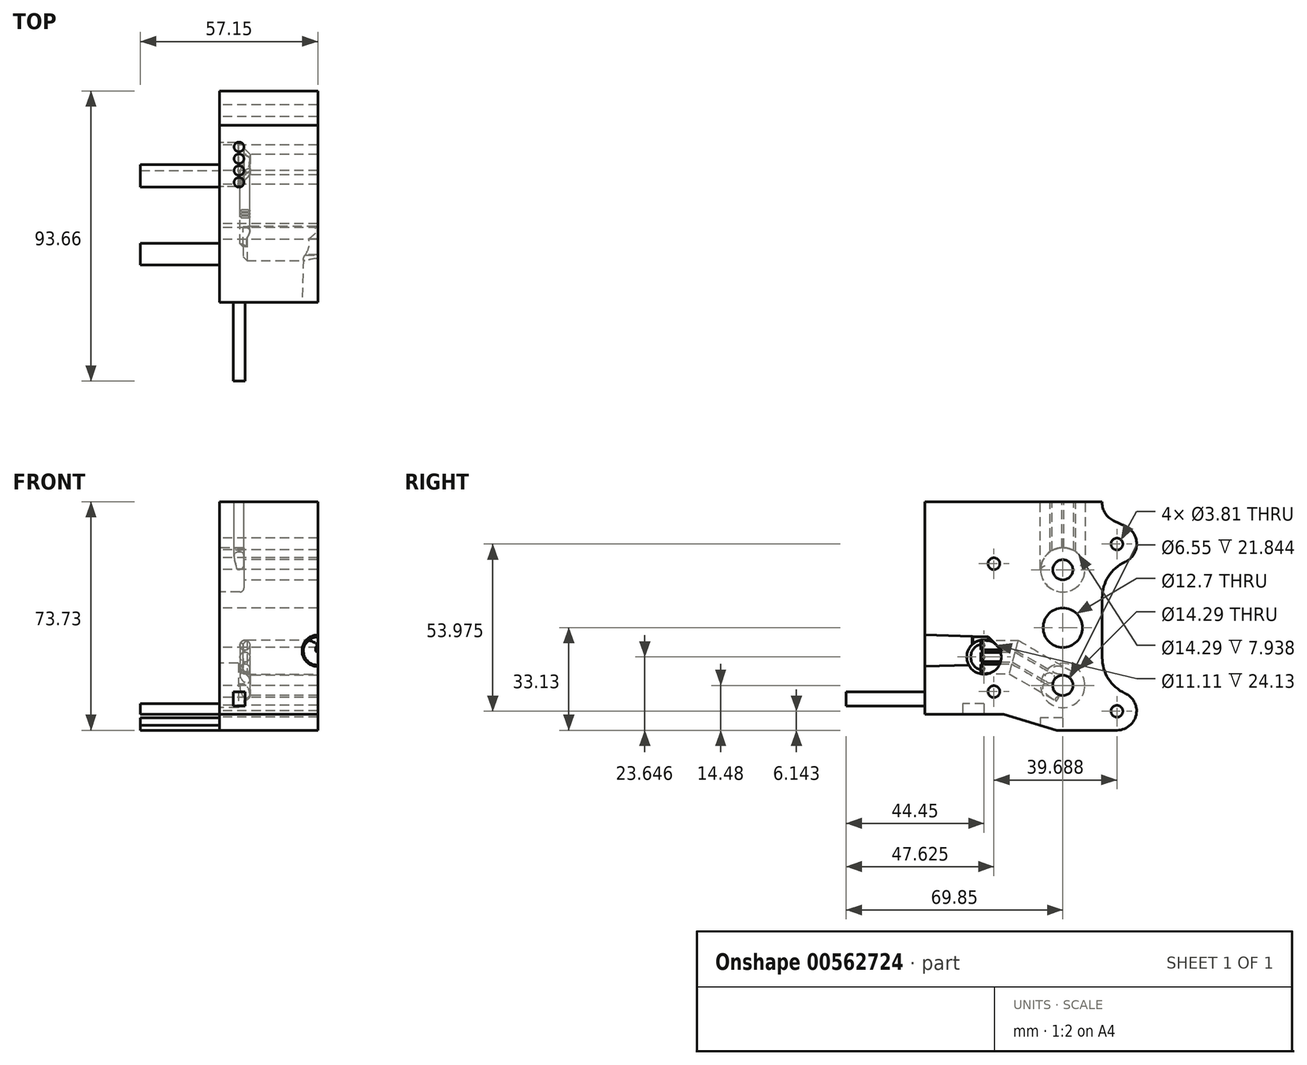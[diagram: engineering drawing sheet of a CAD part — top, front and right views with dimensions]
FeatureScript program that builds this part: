
annotation { "Feature Type Name" : "Feature", "Feature Type Description" : "" }
export const myFeature = defineFeature(function(context is Context, id is Id, definition is map)
    precondition{}
    {
        {
            var Q0;
            Q0=qCreatedBy(makeId("Front.planeOp"),FACE);
            var sketch = newSketch(context, id + "F0", { "sketchPlane" : qUnion([Q0])});
            skLineSegment(sketch, "E0.bottom", {"start": v(-31.75, 40.6) * mm, "end": v(31.75, 40.6) * mm});
            skLineSegment(sketch, "E0.top", {"start": v(-31.75, -35.6) * mm, "end": v(31.75, -35.6) * mm});
            skLineSegment(sketch, "E0.left", {"start": v(-31.75, 40.6) * mm, "end": v(-31.75, -35.6) * mm});
            skLineSegment(sketch, "E0.right", {"start": v(31.75, 40.6) * mm, "end": v(31.75, -35.6) * mm});
            skSolve(sketch);
        }
        {
            var Q0;
            Q0=makeQuery(id+"F0.imprint","IMPRINT",FACE,{"disambiguationData":[TD([[makeQuery(id+"F0.imprint","IMPRINT",EDGE,{"derivedFrom":sQuery(id+"F0.wireOp",EDGE,"E0.bottom")}),-1.0]])]});
            extrude(context, id + "F1", {"entities" : qUnion([Q0]), "depth" : 76.2 * mm, "offsetDistance" : 25.4 * mm});
        }
        {
            var Q0;
            Q0=makeQuery(id+"F1.opExtrude","SWEPT_FACE",FACE,{"disambiguationData":[OSD([sQuery(id+"F0.wireOp",EDGE,"E0.left")])]});
            var sketch = newSketch(context, id + "F2", { "sketchPlane" : qUnion([Q0])});
            skCircle(sketch, "E1", {"center": v(31.75, 0) * mm, "radius": 6.35 * mm});
            skCircle(sketch, "E2", {"center": v(31.75, 18.66) * mm, "radius": 7.14 * mm});
            skCircle(sketch, "E3", {"center": v(31.75, -18.65) * mm, "radius": 7.14 * mm});
            skCircle(sketch, "E4", {"center": v(14.29, 26.99) * mm, "radius": 1.9 * mm});
            skCircle(sketch, "E5", {"center": v(14.29, -26.99) * mm, "radius": 1.9 * mm});
            skCircle(sketch, "E6", {"center": v(53.98, -20.64) * mm, "radius": 1.9 * mm});
            skCircle(sketch, "E7", {"center": v(53.97, 20.64) * mm, "radius": 1.9 * mm});
            skCircle(sketch, "E8", {"center": v(31.75, 18.66) * mm, "radius": 3.25 * mm});
            skCircle(sketch, "E9", {"center": v(31.75, -18.65) * mm, "radius": 3.28 * mm});
            skLineSegment(sketch, "E10.bottom", {"start": v(31.75, -29.15) * mm, "end": v(39.04, -29.15) * mm});
            skLineSegment(sketch, "E10.top", {"start": v(31.75, -33.13) * mm, "end": v(39.04, -33.13) * mm});
            skLineSegment(sketch, "E10.left", {"start": v(31.75, -29.15) * mm, "end": v(31.75, -33.13) * mm});
            skLineSegment(sketch, "E10.right", {"start": v(39.04, -29.15) * mm, "end": v(39.04, -33.13) * mm});
            skLineSegment(sketch, "E11.bottom", {"start": v(57.15, -24.55) * mm, "end": v(64.1, -24.55) * mm});
            skLineSegment(sketch, "E11.top", {"start": v(57.15, -30.95) * mm, "end": v(64.1, -30.95) * mm});
            skLineSegment(sketch, "E11.left", {"start": v(57.15, -24.55) * mm, "end": v(57.15, -30.95) * mm});
            skLineSegment(sketch, "E11.right", {"start": v(64.1, -24.55) * mm, "end": v(64.1, -30.95) * mm});
            skCircle(sketch, "E12", {"center": v(31.75, -18.65) * mm, "radius": 5.56 * mm});
            skLineSegment(sketch, "E13", {"start": v(25.4, -35.6) * mm, "end": v(50.8, -27.98) * mm});
            skLineSegment(sketch, "E14", {"start": v(50.8, -27.98) * mm, "end": v(76.2, -27.98) * mm});
            skSolve(sketch);
        }
        {
            var Q0;
            Q0=makeQuery(id+"F2.imprint","IMPRINT",FACE,{"disambiguationData":[TD([[makeQuery(id+"F2.imprint","IMPRINT",EDGE,{"derivedFrom":sQuery(id+"F2.wireOp",EDGE,"E8")}),1.0]])]});
            var Q1;
            Q1=makeQuery(id+"F2.imprint","IMPRINT",FACE,{"disambiguationData":[TD([[makeQuery(id+"F2.imprint","IMPRINT",EDGE,{"derivedFrom":sQuery(id+"F2.wireOp",EDGE,"E4")}),1.0]])]});
            var Q2;
            Q2=makeQuery(id+"F2.imprint","IMPRINT",FACE,{"disambiguationData":[TD([[makeQuery(id+"F2.imprint","IMPRINT",EDGE,{"derivedFrom":sQuery(id+"F2.wireOp",EDGE,"E5")}),1.0]])]});
            var Q3;
            Q3=makeQuery(id+"F2.imprint","IMPRINT",FACE,{"disambiguationData":[TD([[makeQuery(id+"F2.imprint","IMPRINT",EDGE,{"derivedFrom":sQuery(id+"F2.wireOp",EDGE,"E9")}),1.0]])]});
            var Q4;
            Q4=makeQuery(id+"F2.imprint","IMPRINT",FACE,{"disambiguationData":[TD([[makeQuery(id+"F2.imprint","IMPRINT",EDGE,{"derivedFrom":sQuery(id+"F2.wireOp",EDGE,"E6")}),1.0]])]});
            var Q5;
            Q5=makeQuery(id+"F2.imprint","IMPRINT",FACE,{"disambiguationData":[TD([[makeQuery(id+"F2.imprint","IMPRINT",EDGE,{"derivedFrom":sQuery(id+"F2.wireOp",EDGE,"E7")}),1.0]])]});
            var Q6;
            Q6=makeQuery(id+"F2.imprint","IMPRINT",FACE,{"disambiguationData":[TD([[makeQuery(id+"F2.imprint","IMPRINT",EDGE,{"derivedFrom":sQuery(id+"F2.wireOp",EDGE,"E1")}),1.0]])]});
            extrude(context, id + "F3", {"entities" : qUnion([Q0, Q1, Q2, Q3, Q4, Q5, Q6]), "operationType" : NewBodyOperationType.REMOVE, "endBound" : BoundingType.THROUGH_ALL, "oppositeDirection" : true, "depth" : 25.4 * mm, "offsetDistance" : 25.4 * mm});
        }
        {
            var Q0;
            Q0=makeQuery(id+"F2.imprint","IMPRINT",FACE,{"disambiguationData":[TD([[makeQuery(id+"F2.imprint","IMPRINT",EDGE,{"derivedFrom":sQuery(id+"F2.wireOp",EDGE,"E10.bottom")}),-1.0]])]});
            extrude(context, id + "F4", {"entities" : qUnion([Q0]), "depth" : 25.4 * mm, "offsetDistance" : 25.4 * mm});
        }
        {
            var Q0;
            Q0=makeQuery(id+"F2.imprint","IMPRINT",FACE,{"disambiguationData":[TD([[makeQuery(id+"F2.imprint","IMPRINT",EDGE,{"derivedFrom":sQuery(id+"F2.wireOp",EDGE,"E11.bottom")}),-1.0]])]});
            extrude(context, id + "F5", {"entities" : qUnion([Q0]), "depth" : 25.4 * mm, "offsetDistance" : 25.4 * mm});
        }
        {
            var Q0;
            Q0=makeQuery(id+"F1.opExtrude","CAP_FACE",FACE,{"disambiguationData":[OSD([sQuery(id+"F0.wireOp",EDGE,"E0.bottom"),sQuery(id+"F0.wireOp",EDGE,"E0.top"),sQuery(id+"F0.wireOp",EDGE,"E0.left"),sQuery(id+"F0.wireOp",EDGE,"E0.right")])],"isStart":false});
            var sketch = newSketch(context, id + "F6", { "sketchPlane" : qUnion([Q0])});
            skLineSegment(sketch, "E15.bottom", {"start": v(-27.25, -20.74) * mm, "end": v(-23.5, -20.74) * mm});
            skLineSegment(sketch, "E15.top", {"start": v(-27.25, -25.26) * mm, "end": v(-23.5, -25.26) * mm});
            skLineSegment(sketch, "E15.left", {"start": v(-27.25, -20.74) * mm, "end": v(-27.25, -25.26) * mm});
            skLineSegment(sketch, "E15.right", {"start": v(-23.5, -20.74) * mm, "end": v(-23.5, -25.26) * mm});
            skSolve(sketch);
        }
        {
            var Q0;
            Q0=makeQuery(id+"F6.imprint","IMPRINT",FACE,{"disambiguationData":[TD([[makeQuery(id+"F6.imprint","IMPRINT",EDGE,{"derivedFrom":sQuery(id+"F6.wireOp",EDGE,"E15.bottom")}),-1.0]])]});
            extrude(context, id + "F7", {"entities" : qUnion([Q0]), "depth" : 25.4 * mm, "offsetDistance" : 25.4 * mm});
        }
        {
            var Q0;
            Q0=makeQuery(id+"F4.opExtrude","SWEPT_FACE",FACE,{"disambiguationData":[OSD([sQuery(id+"F2.wireOp",EDGE,"E10.left")])]});
            var sketch = newSketch(context, id + "F8", { "sketchPlane" : qUnion([Q0])});
            skLineSegment(sketch, "E16", {"start": v(31.75, -18.65) * mm, "end": v(23.5, -18.65) * mm});
            skSolve(sketch);
        }
        {
            var Q0;
            Q0=makeQuery(id+"F7.opExtrude","SWEPT_FACE",FACE,{"disambiguationData":[OSD([sQuery(id+"F6.wireOp",EDGE,"E15.right")])]});
            var sketch = newSketch(context, id + "F9", { "sketchPlane" : qUnion([Q0])});
            skLineSegment(sketch, "E17", {"start": v(-31.75, -18.65) * mm, "end": v(-47.62, -9.48) * mm});
            skLineSegment(sketch, "E18", {"start": v(-47.62, -9.48) * mm, "end": v(-57.15, -9.48) * mm});
            skLineSegment(sketch, "E19", {"start": v(-29.92, -15.3) * mm, "end": v(-46.6, -5.67) * mm});
            skLineSegment(sketch, "E20", {"start": v(-33.04, -22.3) * mm, "end": v(-48.65, -13.3) * mm});
            skLineSegment(sketch, "E21", {"start": v(-46.6, -5.67) * mm, "end": v(-57.15, -5.67) * mm});
            skLineSegment(sketch, "E22", {"start": v(-48.65, -13.3) * mm, "end": v(-57.15, -13.3) * mm});
            skSolve(sketch);
        }
        {
            var Q0;
            Q0=makeQuery(id+"F5.opExtrude","SWEPT_FACE",FACE,{"disambiguationData":[OSD([sQuery(id+"F2.wireOp",EDGE,"E11.left")])]});
            var sketch = newSketch(context, id + "F10", { "sketchPlane" : qUnion([Q0])});
            skLineSegment(sketch, "E23", {"start": v(23.5, -9.48) * mm, "end": v(0, -9.48) * mm});
            skCircle(sketch, "E24", {"center": v(23.5, -9.48) * mm, "radius": 1.59 * mm});
            skCircle(sketch, "E25", {"center": v(23.5, -5.67) * mm, "radius": 1.59 * mm});
            skCircle(sketch, "E26", {"center": v(23.5, -13.3) * mm, "radius": 1.59 * mm});
            skSolve(sketch);
        }
        {
            var Q0;
            Q0=makeQuery(id+"F2.imprint","IMPRINT",FACE,{"disambiguationData":[TD([[makeQuery(id+"F2.imprint","IMPRINT",EDGE,{"derivedFrom":sQuery(id+"F2.wireOp",EDGE,"E3")}),1.0]])]});
            var Q1;
            Q1=makeQuery(id+"F2.imprint","IMPRINT",FACE,{"disambiguationData":[TD([[makeQuery(id+"F2.imprint","IMPRINT",EDGE,{"derivedFrom":sQuery(id+"F2.wireOp",EDGE,"E9")}),-1.0]])]});
            var Q2;
            Q2=sQuery(id+"F9.wireOp",VERTEX,"E17.start");
            extrude(context, id + "F11", {"entities" : qUnion([Q0, Q1]), "operationType" : NewBodyOperationType.REMOVE, "oppositeDirection" : true, "depth" : 9.9 * mm, "endBoundEntityVertex" : qUnion([Q2]), "offsetDistance" : 25.4 * mm});
        }
        {
            var Q0;
            Q0=makeQuery(id+"F11.boolean.opBoolean","COPY",EDGE,{"derivedFrom":makeQuery(id+"F11.opExtrude","CAP_EDGE",EDGE,{"disambiguationData":[OSD([sQuery(id+"F2.wireOp",EDGE,"E3")])],"isStart":false})});
            chamfer(context, id + "F12", {"entities" : qUnion([Q0]), "width" : 3.8 * mm, "tangentPropagation" : true});
        }
        {
            var Q0;
            {var subQ0=sQuery(id+"F2.wireOp",EDGE,"E10.right");var subQ1=sQuery(id+"F2.wireOp",EDGE,"E10.top");var subQ2=makeQuery(id+"F2.imprint","INTERSECT",VERTEX,{"derivedFrom":[subQ1,subQ0]});Q0=makeQuery(id+"F2.imprint","IMPRINT",FACE,{"disambiguationData":[TD([[makeQuery(id+"F2.imprint","IMPRINT",EDGE,{"disambiguationData":[TD([[subQ2,1.0]])],"derivedFrom":subQ1}),1.0]])]});}
            var Q1;
            {var subQ11=sQuery(id+"F2.wireOp",EDGE,"E11.top");Q1=makeQuery(id+"F2.imprint","IMPRINT",FACE,{"disambiguationData":[TD([[makeQuery(id+"F2.imprint","IMPRINT",EDGE,{"derivedFrom":subQ11}),-1.0]])]});}
            var Q2;
            {var subQ0=sQuery(id+"F2.wireOp",EDGE,"E11.top");Q2=makeQuery(id+"F2.imprint","IMPRINT",FACE,{"disambiguationData":[TD([[makeQuery(id+"F2.imprint","IMPRINT",EDGE,{"derivedFrom":subQ0}),1.0]])]});}
            extrude(context, id + "F13", {"entities" : qUnion([Q0, Q1, Q2]), "operationType" : NewBodyOperationType.REMOVE, "endBound" : BoundingType.THROUGH_ALL, "oppositeDirection" : true, "depth" : 25.4 * mm, "offsetDistance" : 25.4 * mm});
        }
        {
            var Q0;
            Q0=makeQuery(id+"F1.opExtrude","CAP_FACE",FACE,{"disambiguationData":[OSD([sQuery(id+"F0.wireOp",EDGE,"E0.bottom"),sQuery(id+"F0.wireOp",EDGE,"E0.top"),sQuery(id+"F0.wireOp",EDGE,"E0.left"),sQuery(id+"F0.wireOp",EDGE,"E0.right")])],"isStart":false});
            var sketch = newSketch(context, id + "F14", { "sketchPlane" : qUnion([Q0])});
            skCircle(sketch, "E27", {"center": v(0, -7.45) * mm, "radius": 4.45 * mm});
            skCircle(sketch, "E28", {"center": v(0, 9.57) * mm, "radius": 3.81 * mm});
            skSolve(sketch);
        }
        {
            var Q0;
            Q0=makeQuery(id+"F14.imprint","IMPRINT",FACE,{"disambiguationData":[TD([[makeQuery(id+"F14.imprint","IMPRINT",EDGE,{"derivedFrom":sQuery(id+"F14.wireOp",EDGE,"E27")}),1.0]])]});
            extrude(context, id + "F15", {"entities" : qUnion([Q0]), "operationType" : NewBodyOperationType.REMOVE, "oppositeDirection" : true, "depth" : 24.76 * mm, "offsetDistance" : 25.4 * mm});
        }
        {
            var Q0;
            Q0=qCreatedBy(makeId("Right.planeOp"),FACE);
            var sketch = newSketch(context, id + "F16", { "sketchPlane" : qUnion([Q0])});
            skLineSegment(sketch, "E29", {"start": v(-76.17, -12.53) * mm, "end": v(-60.94, -12.06) * mm});
            skLineSegment(sketch, "E30", {"start": v(-60.94, -12.06) * mm, "end": v(-60.15, -11.26) * mm});
            skLineSegment(sketch, "E31", {"start": v(-76.2, -11.26) * mm, "end": v(-60.15, -11.26) * mm});
            skLineSegment(sketch, "E32", {"start": v(-76.2, -7.45) * mm, "end": v(-74.2, -7.45) * mm});
            skLineSegment(sketch, "E33", {"start": v(-76.17, -12.53) * mm, "end": v(-76.34, -12.54) * mm});
            skLineSegment(sketch, "E34", {"start": v(-76.34, -12.54) * mm, "end": v(-76.34, -11.26) * mm});
            skLineSegment(sketch, "E35", {"start": v(-76.34, -11.26) * mm, "end": v(-76.2, -11.26) * mm});
            skSolve(sketch);
        }
        {
            var Q0;
            Q0 = qSketchRegion(id + "F16", true);
            var Q1;
            Q1=sQuery(id+"F16.wireOp",EDGE,"E32");
            revolve(context, id + "F17", {"operationType" : NewBodyOperationType.REMOVE, "entities" : qUnion([Q0]), "axis" : qUnion([Q1]), "revolveType" : RevolveType.FULL, "oppositeDirection" : true});
        }
        {
            var Q0;
            Q0=makeQuery(id+"F1.opExtrude","SWEPT_FACE",FACE,{"disambiguationData":[OSD([sQuery(id+"F0.wireOp",EDGE,"E0.right")])]});
            extrude(context, id + "F18", {"entities" : qUnion([Q0]), "operationType" : NewBodyOperationType.REMOVE, "oppositeDirection" : true, "depth" : 31.75 * mm, "offsetDistance" : 25.4 * mm});
        }
        {
            var Q0;
            Q0=makeQuery(id+"F15.boolean.opBoolean","COPY",EDGE,{"derivedFrom":makeQuery(id+"F15.opExtrude","CAP_EDGE",EDGE,{"disambiguationData":[OSD([sQuery(id+"F14.wireOp",EDGE,"E27")])],"isStart":false})});
            chamfer(context, id + "F19", {"entities" : qUnion([Q0]), "width" : 4.32 * mm, "tangentPropagation" : true});
        }
        {
            var Q0;
            Q0=makeQuery(id+"F4.opExtrude","SWEPT_FACE",FACE,{"disambiguationData":[OSD([sQuery(id+"F2.wireOp",EDGE,"E10.left")])]});
            var sketch = newSketch(context, id + "F20", { "sketchPlane" : qUnion([Q0])});
            skLineSegment(sketch, "E36", {"start": v(31.75, 18.66) * mm, "end": v(25.4, 18.66) * mm});
            skLineSegment(sketch, "E37", {"start": v(25.4, 18.66) * mm, "end": v(25.4, 40.6) * mm});
            skSolve(sketch);
        }
        {
            var Q0;
            Q0=makeQuery(id+"F1.opExtrude","SWEPT_FACE",FACE,{"disambiguationData":[OSD([sQuery(id+"F0.wireOp",EDGE,"E0.bottom")])]});
            var sketch = newSketch(context, id + "F21", { "sketchPlane" : qUnion([Q0])});
            skCircle(sketch, "E38", {"center": v(-25.4, -29.84) * mm, "radius": 1.59 * mm});
            skCircle(sketch, "E39", {"center": v(-25.4, -33.65) * mm, "radius": 1.59 * mm});
            skCircle(sketch, "E40", {"center": v(-25.4, -26.04) * mm, "radius": 1.59 * mm});
            skCircle(sketch, "E41", {"center": v(-25.4, -37.46) * mm, "radius": 1.59 * mm});
            skSolve(sketch);
        }
        {
            var Q0;
            Q0=makeQuery(id+"F21.imprint","IMPRINT",FACE,{"disambiguationData":[TD([[makeQuery(id+"F21.imprint","IMPRINT",EDGE,{"derivedFrom":sQuery(id+"F21.wireOp",EDGE,"E40")}),1.0]])]});
            var Q1;
            Q1=makeQuery(id+"F21.imprint","IMPRINT",FACE,{"disambiguationData":[TD([[makeQuery(id+"F21.imprint","IMPRINT",EDGE,{"derivedFrom":sQuery(id+"F21.wireOp",EDGE,"E38")}),1.0]])]});
            var Q2;
            Q2=makeQuery(id+"F21.imprint","IMPRINT",FACE,{"disambiguationData":[TD([[makeQuery(id+"F21.imprint","IMPRINT",EDGE,{"derivedFrom":sQuery(id+"F21.wireOp",EDGE,"E39")}),1.0]])]});
            var Q3;
            Q3=makeQuery(id+"F21.imprint","IMPRINT",FACE,{"disambiguationData":[TD([[makeQuery(id+"F21.imprint","IMPRINT",EDGE,{"derivedFrom":sQuery(id+"F21.wireOp",EDGE,"E41")}),1.0]])]});
            var Q4;
            Q4=sQuery(id+"F2.wireOp",VERTEX,"E8.center");
            extrude(context, id + "F22", {"entities" : qUnion([Q0, Q1, Q2, Q3]), "operationType" : NewBodyOperationType.REMOVE, "endBound" : BoundingType.UP_TO_VERTEX, "oppositeDirection" : true, "depth" : 25.4 * mm, "endBoundEntityVertex" : qUnion([Q4]), "offsetDistance" : 25.4 * mm});
        }
        {
            var Q0;
            Q0=makeQuery(id+"F2.imprint","IMPRINT",FACE,{"disambiguationData":[TD([[makeQuery(id+"F2.imprint","IMPRINT",EDGE,{"derivedFrom":sQuery(id+"F2.wireOp",EDGE,"E2")}),1.0]])]});
            extrude(context, id + "F23", {"entities" : qUnion([Q0]), "operationType" : NewBodyOperationType.REMOVE, "oppositeDirection" : true, "depth" : 7.94 * mm, "offsetDistance" : 25.4 * mm});
        }
        {
            var Q0;
            Q0=makeQuery(id+"F22.boolean.opBoolean","COPY",EDGE,{"derivedFrom":makeQuery(id+"F22.opExtrude","CAP_EDGE",EDGE,{"disambiguationData":[OSD([sQuery(id+"F21.wireOp",EDGE,"E40")])],"isStart":false})});
            var Q1;
            Q1=makeQuery(id+"F22.boolean.opBoolean","COPY",EDGE,{"derivedFrom":makeQuery(id+"F22.opExtrude","CAP_EDGE",EDGE,{"disambiguationData":[OSD([sQuery(id+"F21.wireOp",EDGE,"E41")])],"isStart":false})});
            chamfer(context, id + "F24", {"entities" : qUnion([Q0, Q1]), "width" : 0.25 * mm, "tangentPropagation" : true});
        }
        {
            var Q0;
            {var subQ0=sQuery(id+"F2.wireOp",EDGE,"E2");Q0=makeQuery(id+"F23.boolean.opBoolean","COPY",EDGE,{"disambiguationData":[TD([makeQuery(id+"F22.boolean.opBoolean","COPY",FACE,{"derivedFrom":makeQuery(id+"F22.opExtrude","SWEPT_FACE",FACE,{"disambiguationData":[OSD([sQuery(id+"F21.wireOp",EDGE,"E40")])]})}),makeQuery(id+"F22.boolean.opBoolean","COPY",FACE,{"derivedFrom":makeQuery(id+"F22.opExtrude","SWEPT_FACE",FACE,{"disambiguationData":[OSD([sQuery(id+"F21.wireOp",EDGE,"E41")])]})}),makeQuery(id+"F23.opExtrude","SWEPT_FACE",FACE,{"disambiguationData":[OSD([subQ0])]}),makeQuery(id+"F23.opExtrude","CAP_FACE",FACE,{"disambiguationData":[OSD([subQ0,sQuery(id+"F2.wireOp",EDGE,"E8")])],"isStart":false})])],"derivedFrom":makeQuery(id+"F23.opExtrude","CAP_EDGE",EDGE,{"disambiguationData":[OSD([subQ0])],"isStart":false})});}
            fillet(context, id + "F25", {"entities" : qUnion([Q0]), "radius" : 1.27 * mm, "allowEdgeOverflow" : false});
        }
        {
            var Q0;
            Q0=makeQuery(id+"F2.imprint","IMPRINT",FACE,{"disambiguationData":[TD([[makeQuery(id+"F2.imprint","IMPRINT",EDGE,{"derivedFrom":sQuery(id+"F2.wireOp",EDGE,"E1")}),-1.0]])]});
            var sketch = newSketch(context, id + "F26", { "sketchPlane" : qUnion([Q0])});
            skLineSegment(sketch, "E42", {"start": v(7.94, 27) * mm, "end": v(7.94, 26.99) * mm});
            skLineSegment(sketch, "E43", {"start": v(11.6, 21.23) * mm, "end": v(11.72, 21.18) * mm});
            skLineSegment(sketch, "E44", {"start": v(19.05, 9.67) * mm, "end": v(19.05, -9.67) * mm});
            skLineSegment(sketch, "E45", {"start": v(11.72, -21.18) * mm, "end": v(11.6, -21.23) * mm});
            skLineSegment(sketch, "E46", {"start": v(7.94, -26.78) * mm, "end": v(7.94, -26.99) * mm});
            skPoint(sketch, "E47.visualSharp", {"position": v(19.05, 17.76) * mm});
            skArc(sketch, "E47.filletArc", {"start": v(19.05, 9.67) * mm, "mid": v(17.06, 16.5) * mm, "end": v(11.72, 21.18) * mm});
            skPoint(sketch, "E48.visualSharp", {"position": v(19.05, -17.76) * mm});
            skArc(sketch, "E48.filletArc", {"start": v(11.72, -21.18) * mm, "mid": v(17.06, -16.5) * mm, "end": v(19.05, -9.67) * mm});
            skPoint(sketch, "E49.visualSharp", {"position": v(7.94, -22.94) * mm});
            skArc(sketch, "E49.filletArc", {"start": v(11.6, -21.23) * mm, "mid": v(8.93, -23.58) * mm, "end": v(7.94, -26.99) * mm});
            skPoint(sketch, "E50.visualSharp", {"position": v(7.94, 22.94) * mm});
            skArc(sketch, "E50.filletArc", {"start": v(7.94, 26.99) * mm, "mid": v(8.93, 23.58) * mm, "end": v(11.6, 21.23) * mm});
            skLineSegment(sketch, "E51", {"start": v(11.6, 32.76) * mm, "end": v(15.38, 34.52) * mm});
            skLineSegment(sketch, "E52", {"start": v(19.05, 40.28) * mm, "end": v(19.05, 40.6) * mm});
            skPoint(sketch, "E53.newPointA", {"position": v(7.94, 31.05) * mm});
            skPoint(sketch, "E53.newPointB", {"position": v(7.94, 40.6) * mm});
            skArc(sketch, "E53.filletArc", {"start": v(11.6, 32.76) * mm, "mid": v(8.93, 30.42) * mm, "end": v(7.94, 27) * mm});
            skPoint(sketch, "E54.visualSharp", {"position": v(19.05, 36.23) * mm});
            skArc(sketch, "E54.filletArc", {"start": v(15.38, 34.52) * mm, "mid": v(18.06, 36.87) * mm, "end": v(19.05, 40.28) * mm});
            skLineSegment(sketch, "E55", {"start": v(14.29, -33.13) * mm, "end": v(19.83, -33.13) * mm});
            skPoint(sketch, "E56.visualSharp", {"position": v(7.94, -35.6) * mm});
            skArc(sketch, "E56.filletArc", {"start": v(7.94, -26.78) * mm, "mid": v(9.8, -31.27) * mm, "end": v(14.29, -33.13) * mm});
            skLineSegment(sketch, "E57", {"start": v(19.83, -33.13) * mm, "end": v(33.64, -33.13) * mm});
            skLineSegment(sketch, "E58", {"start": v(19.05, 40.6) * mm, "end": v(0, 40.6) * mm});
            skLineSegment(sketch, "E59", {"start": v(0, 40.6) * mm, "end": v(19.05, 40.6) * mm});
            skLineSegment(sketch, "E60", {"start": v(0, 40.6) * mm, "end": v(0, -35.6) * mm});
            skLineSegment(sketch, "E61", {"start": v(0, -35.6) * mm, "end": v(25.4, -35.6) * mm});
            skLineSegment(sketch, "E62", {"start": v(25.4, -35.6) * mm, "end": v(33.64, -33.13) * mm});
            skSolve(sketch);
        }
        {
            var Q0;
            Q0 = qSketchRegion(id + "F26", true);
            extrude(context, id + "F27", {"entities" : qUnion([Q0]), "operationType" : NewBodyOperationType.REMOVE, "endBound" : BoundingType.THROUGH_ALL, "oppositeDirection" : true, "depth" : 25.4 * mm, "offsetDistance" : 25.4 * mm});
        }
        {
            var Q0;
            Q0=makeQuery(id+"F10.imprint","IMPRINT",FACE,{"disambiguationData":[TD([[makeQuery(id+"F10.imprint","IMPRINT",EDGE,{"derivedFrom":sQuery(id+"F10.wireOp",EDGE,"E25")}),1.0]])]});
            var Q1;
            Q1=makeQuery(id+"F10.imprint","IMPRINT",FACE,{"disambiguationData":[TD([[makeQuery(id+"F10.imprint","IMPRINT",EDGE,{"derivedFrom":sQuery(id+"F10.wireOp",EDGE,"E24")}),1.0]])]});
            var Q2;
            Q2=makeQuery(id+"F10.imprint","IMPRINT",FACE,{"disambiguationData":[TD([[makeQuery(id+"F10.imprint","IMPRINT",EDGE,{"derivedFrom":sQuery(id+"F10.wireOp",EDGE,"E26")}),1.0]])]});
            var Q3;
            Q3=sQuery(id+"F9.wireOp",EDGE,"E18");
            var Q4;
            Q4=sQuery(id+"F9.wireOp",EDGE,"E17");
            sweep(context, id + "F28", {"operationType" : NewBodyOperationType.REMOVE, "profiles" : qUnion([Q0, Q1, Q2]), "path" : qUnion([Q3, Q4])});
        }
        {
            var Q0;
            Q0=makeQuery(id+"F18.boolean.opBoolean","COPY",FACE,{"derivedFrom":makeQuery(id+"F18.opExtrude","CAP_FACE",FACE,{"disambiguationData":[OSD([sQuery(id+"F0.wireOp",EDGE,"E0.right")])],"isStart":false})});
            var sketch = newSketch(context, id + "F29", { "sketchPlane" : qUnion([Q0])});
            skCircle(sketch, "E63", {"center": v(-57.15, -9.48) * mm, "radius": 5.56 * mm});
            skSolve(sketch);
        }
        {
            var Q0;
            {var subQ0=makeQuery(id+"F18.opExtrude","CAP_FACE",FACE,{"disambiguationData":[OSD([sQuery(id+"F0.wireOp",EDGE,"E0.right")])],"isStart":false});var subQ1=makeQuery(id+"F18.boolean.opBoolean","INTERSECT",EDGE,{"disambiguationData":[OD(1.0)],"derivedFrom":[makeQuery(id+"F17.boolean.opBoolean","COPY",FACE,{"derivedFrom":makeQuery(id+"F17.opRevolve","SWEPT_FACE",FACE,{"disambiguationData":[OSD([sQuery(id+"F16.wireOp",EDGE,"E30")])]})}),subQ0]});Q0=makeQuery(id+"F29.imprint","IMPRINT",FACE,{"disambiguationData":[TD([[makeQuery(id+"F29.imprint","IMPRINT",EDGE,{"derivedFrom":subQ1}),1.0]])]});}
            var Q1;
            {var subQ0=makeQuery(id+"F18.opExtrude","CAP_FACE",FACE,{"disambiguationData":[OSD([sQuery(id+"F0.wireOp",EDGE,"E0.right")])],"isStart":false});var subQ1=makeQuery(id+"F18.boolean.opBoolean","INTERSECT",EDGE,{"disambiguationData":[OD(1.0)],"derivedFrom":[makeQuery(id+"F17.boolean.opBoolean","COPY",FACE,{"derivedFrom":makeQuery(id+"F17.opRevolve","SWEPT_FACE",FACE,{"disambiguationData":[OSD([sQuery(id+"F16.wireOp",EDGE,"E30")])]})}),subQ0]});Q1=makeQuery(id+"F29.imprint","IMPRINT",FACE,{"disambiguationData":[TD([[makeQuery(id+"F29.imprint","IMPRINT",EDGE,{"derivedFrom":subQ1}),-1.0]])]});}
            extrude(context, id + "F30", {"entities" : qUnion([Q0, Q1]), "operationType" : NewBodyOperationType.REMOVE, "oppositeDirection" : true, "depth" : 24.13 * mm, "offsetDistance" : 25.4 * mm});
        }
        {
            var Q0;
            {var subQ0=sQuery(id+"F9.wireOp",EDGE,"E18");var subQ1=sQuery(id+"F29.wireOp",EDGE,"E63");Q0=makeQuery(id+"F30.boolean.opBoolean","COPY",EDGE,{"disambiguationData":[TD([makeQuery(id+"F28.boolean.opBoolean","COPY",FACE,{"derivedFrom":makeQuery(id+"F28.opSweep","SWEPT_FACE",FACE,{"disambiguationData":[OSD([subQ0,sQuery(id+"F10.wireOp",EDGE,"E25")])]})}),makeQuery(id+"F28.boolean.opBoolean","COPY",FACE,{"derivedFrom":makeQuery(id+"F28.opSweep","SWEPT_FACE",FACE,{"disambiguationData":[OSD([subQ0,sQuery(id+"F10.wireOp",EDGE,"E26")])]})}),makeQuery(id+"F30.opExtrude","SWEPT_FACE",FACE,{"disambiguationData":[OSD([subQ1])]}),makeQuery(id+"F30.opExtrude","CAP_FACE",FACE,{"disambiguationData":[OSD([subQ1])],"isStart":false})])],"derivedFrom":makeQuery(id+"F30.opExtrude","CAP_EDGE",EDGE,{"disambiguationData":[OSD([subQ1])],"isStart":false})});}
            chamfer(context, id + "F31", {"entities" : qUnion([Q0]), "width" : 1.27 * mm, "tangentPropagation" : true});
        }
        {
            var Q0;
            Q0=makeQuery(id+"F30.boolean.opBoolean","INTERSECT",EDGE,{"derivedFrom":[makeQuery(id+"F28.boolean.opBoolean","COPY",FACE,{"derivedFrom":makeQuery(id+"F28.opSweep","CAP_FACE",FACE,{"disambiguationData":[OSD([sQuery(id+"F9.wireOp",VERTEX,"E18.end"),sQuery(id+"F10.wireOp",EDGE,"E24")])],"isStart":true})}),makeQuery(id+"F30.opExtrude","CAP_FACE",FACE,{"disambiguationData":[OSD([sQuery(id+"F29.wireOp",EDGE,"E63")])],"isStart":false})]});
            var Q1;
            Q1=makeQuery(id+"F30.boolean.opBoolean","INTERSECT",EDGE,{"derivedFrom":[makeQuery(id+"F28.boolean.opBoolean","COPY",FACE,{"derivedFrom":makeQuery(id+"F28.opSweep","CAP_FACE",FACE,{"disambiguationData":[OSD([sQuery(id+"F9.wireOp",VERTEX,"E18.end"),sQuery(id+"F10.wireOp",EDGE,"E25")])],"isStart":true})}),makeQuery(id+"F30.opExtrude","CAP_FACE",FACE,{"disambiguationData":[OSD([sQuery(id+"F29.wireOp",EDGE,"E63")])],"isStart":false})]});
            var Q2;
            Q2=makeQuery(id+"F30.boolean.opBoolean","INTERSECT",EDGE,{"derivedFrom":[makeQuery(id+"F28.boolean.opBoolean","COPY",FACE,{"derivedFrom":makeQuery(id+"F28.opSweep","CAP_FACE",FACE,{"disambiguationData":[OSD([sQuery(id+"F9.wireOp",VERTEX,"E18.end"),sQuery(id+"F10.wireOp",EDGE,"E26")])],"isStart":true})}),makeQuery(id+"F30.opExtrude","CAP_FACE",FACE,{"disambiguationData":[OSD([sQuery(id+"F29.wireOp",EDGE,"E63")])],"isStart":false})]});
            chamfer(context, id + "F32", {"entities" : qUnion([Q0, Q1, Q2]), "width" : 1.02 * mm, "tangentPropagation" : true});
        }
        {
            var Q0;
            {var subQ0=sQuery(id+"F10.wireOp",EDGE,"E25");var subQ1=sQuery(id+"F9.wireOp",EDGE,"E18");var subQ2=sQuery(id+"F29.wireOp",EDGE,"E63");Q0=makeQuery(id+"F31.opChamfer","BLEND_EDGE",EDGE,{"blendedFrom":[makeQuery(id+"F30.boolean.opBoolean","COPY",EDGE,{"disambiguationData":[TD([makeQuery(id+"F28.boolean.opBoolean","COPY",FACE,{"derivedFrom":makeQuery(id+"F28.opSweep","SWEPT_FACE",FACE,{"disambiguationData":[OSD([subQ1,subQ0])]})}),makeQuery(id+"F28.boolean.opBoolean","COPY",FACE,{"derivedFrom":makeQuery(id+"F28.opSweep","SWEPT_FACE",FACE,{"disambiguationData":[OSD([subQ1,sQuery(id+"F10.wireOp",EDGE,"E26")])]})}),makeQuery(id+"F30.opExtrude","SWEPT_FACE",FACE,{"disambiguationData":[OSD([subQ2])]}),makeQuery(id+"F30.opExtrude","CAP_FACE",FACE,{"disambiguationData":[OSD([subQ2])],"isStart":false})])],"derivedFrom":makeQuery(id+"F30.opExtrude","CAP_EDGE",EDGE,{"disambiguationData":[OSD([subQ2])],"isStart":false})}),makeQuery(id+"F28.boolean.opBoolean","COPY",FACE,{"derivedFrom":makeQuery(id+"F28.opSweep","CAP_FACE",FACE,{"disambiguationData":[OSD([sQuery(id+"F9.wireOp",VERTEX,"E18.end"),subQ0])],"isStart":true})})],"blendedInto":[makeQuery(id+"F28.boolean.opBoolean","COPY",FACE,{"derivedFrom":makeQuery(id+"F28.opSweep","CAP_FACE",FACE,{"disambiguationData":[OSD([sQuery(id+"F9.wireOp",VERTEX,"E18.end"),subQ0])],"isStart":true})})]});}
            var Q1;
            {var subQ0=sQuery(id+"F10.wireOp",EDGE,"E26");var subQ1=sQuery(id+"F9.wireOp",EDGE,"E18");var subQ2=sQuery(id+"F29.wireOp",EDGE,"E63");Q1=makeQuery(id+"F31.opChamfer","BLEND_EDGE",EDGE,{"blendedFrom":[makeQuery(id+"F30.boolean.opBoolean","COPY",EDGE,{"disambiguationData":[TD([makeQuery(id+"F28.boolean.opBoolean","COPY",FACE,{"derivedFrom":makeQuery(id+"F28.opSweep","SWEPT_FACE",FACE,{"disambiguationData":[OSD([subQ1,sQuery(id+"F10.wireOp",EDGE,"E25")])]})}),makeQuery(id+"F28.boolean.opBoolean","COPY",FACE,{"derivedFrom":makeQuery(id+"F28.opSweep","SWEPT_FACE",FACE,{"disambiguationData":[OSD([subQ1,subQ0])]})}),makeQuery(id+"F30.opExtrude","SWEPT_FACE",FACE,{"disambiguationData":[OSD([subQ2])]}),makeQuery(id+"F30.opExtrude","CAP_FACE",FACE,{"disambiguationData":[OSD([subQ2])],"isStart":false})])],"derivedFrom":makeQuery(id+"F30.opExtrude","CAP_EDGE",EDGE,{"disambiguationData":[OSD([subQ2])],"isStart":false})}),makeQuery(id+"F28.boolean.opBoolean","COPY",FACE,{"derivedFrom":makeQuery(id+"F28.opSweep","CAP_FACE",FACE,{"disambiguationData":[OSD([sQuery(id+"F9.wireOp",VERTEX,"E18.end"),subQ0])],"isStart":true})})],"blendedInto":[makeQuery(id+"F28.boolean.opBoolean","COPY",FACE,{"derivedFrom":makeQuery(id+"F28.opSweep","CAP_FACE",FACE,{"disambiguationData":[OSD([sQuery(id+"F9.wireOp",VERTEX,"E18.end"),subQ0])],"isStart":true})})]});}
            chamfer(context, id + "F33", {"entities" : qUnion([Q0, Q1]), "width" : 1.27 * mm, "tangentPropagation" : true});
        }
        {
            var Q0;
            Q0=makeQuery(id+"F28.boolean.opBoolean","INTERSECT",EDGE,{"derivedFrom":[makeQuery(id+"F12.opChamfer","BLEND_FACE",FACE,{"disambiguationData":[OSD([sQuery(id+"F2.wireOp",EDGE,"E3")])]}),makeQuery(id+"F28.opSweep","CAP_FACE",FACE,{"disambiguationData":[OSD([sQuery(id+"F9.wireOp",VERTEX,"E17.start"),sQuery(id+"F10.wireOp",EDGE,"E25")])],"isStart":false})]});
            var Q1;
            Q1=makeQuery(id+"F28.boolean.opBoolean","INTERSECT",EDGE,{"derivedFrom":[makeQuery(id+"F12.opChamfer","BLEND_FACE",FACE,{"disambiguationData":[OSD([sQuery(id+"F2.wireOp",EDGE,"E3")])]}),makeQuery(id+"F28.opSweep","CAP_FACE",FACE,{"disambiguationData":[OSD([sQuery(id+"F9.wireOp",VERTEX,"E17.start"),sQuery(id+"F10.wireOp",EDGE,"E26")])],"isStart":false})]});
            chamfer(context, id + "F34", {"entities" : qUnion([Q0, Q1]), "width" : 0.89 * mm, "tangentPropagation" : true});
        }
    });
